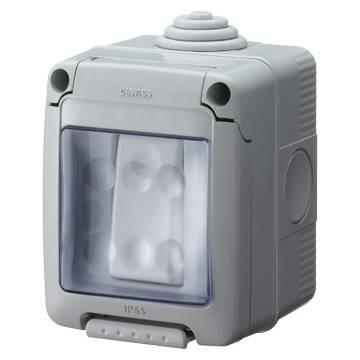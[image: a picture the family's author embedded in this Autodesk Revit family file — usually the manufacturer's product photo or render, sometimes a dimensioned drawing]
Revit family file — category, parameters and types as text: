
# Revit family: Domotics-SerieCivili-GEWISS-27COMBI_SYSTEM-IP55_COMANDO_1M
name_source: partatom
category: Apparecchi elettrici
revit_build: Autodesk Revit 2016 (Build: 20161004_0715(x64)
units: mm (PartAtom-declared; Revit-internal decimal feet)

## family parameters
Condiviso = Sì
Host = Superficie
Mantenere orientamento annotazione = Sì
Numero OmniClass = 23.80.50.11.14
Punto di calcolo locali = No
Quota connettore circolare = Usa diametro
Taglio con vuoti quando caricato = Sì
Tipo di parte = Normale
Titolo OmniClass = Switches

## types (1)
- Domotics-SerieCivili-GEWISS-27COMBI_SYSTEM-IP55_COMANDO_1M
    Catalogo = DOMOTICS
    Catalogo Serie = 27COMBI
    Classe isolamento = II
    Classificazione = Altro
    Codice EAN = 8011564095441
    Codice Electrocod = 0130
    Colore = Grigio RAL 7035
    Colore portella = Trasparente
    Coppia serraggio viti = 0,8NM
    Descrizione = PULSANTE UNIP.10A STAGNO
    Descrizione: = Pulsante 1P NA - 10 A
    Dim. esterne BxHxP (mm) = 66x82x65
    Glow Wire Test = 650°C
    Grado di protezione = IP55
    IDF = 93e6e43b-348a-40b4-8470-7bf0be55fd67
    IDT = 2d0f21d1-8ef9-4ef1-9a1b-35e0feede76f
    Immagine tipo = GW27835.jpg
    Modello = GW27835
    N. fori Ã˜ 23 con passacavo = 1
    N. fori Ã˜ 23 sfondabili: = Laterali 3 / Sul fondo 1
    Norma di riferimento: = EN 60669-1
    Offset = 0 mm  [stored 0 ft]
    Produttore = GEWISS S.p.A.
    Prospetto di default = 1219 mm
    SEO = Contenitore
    Scheda Tecnica = https://www.gewiss.com
    Temperatura di installazione = -25 +60 °C
    Tensione = 230 V ac
    Tensione: = 250 V ac
    Termopressione con biglia = 70 °C
    Tipo = Pulsante 1P NA - 10 A
    Tipo portella = Con membrana
    Tipo sfondabili = Asportabili con utensile
    Tipo simbolo = SIMBOLO PULSANTI : PULSANTE
    URL = https://www.gewiss.com
    Versione file RFA = 19.4
    Vetrino luminoso = Sì
    Viti coperchio = Acciaio inox

note: [stored X ft] marks values corroborated as IEEE doubles in the binary element streams (Revit-internal decimal feet)

## geometry (parser evidence)
native form markers: Sweep x4
no freeform markers — native parametric forms only
